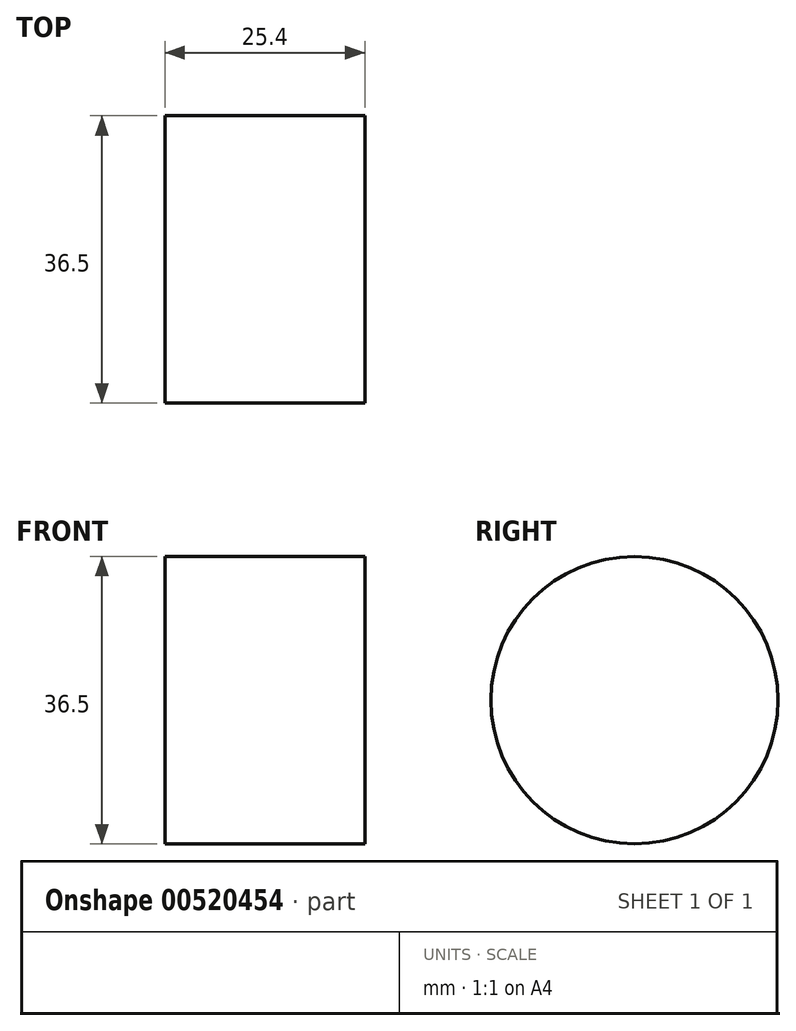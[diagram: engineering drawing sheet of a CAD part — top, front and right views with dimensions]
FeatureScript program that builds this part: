
annotation { "Feature Type Name" : "Feature", "Feature Type Description" : "" }
export const myFeature = defineFeature(function(context is Context, id is Id, definition is map)
    precondition{}
    {
        {
            var Q0;
            Q0=qCreatedBy(makeId("Right.planeOp"),FACE);
            var sketch = newSketch(context, id + "F0", { "sketchPlane" : qUnion([Q0])});
            skCircle(sketch, "E0", {"center": v(0, 0) * mm, "radius": 18.25 * mm});
            skSolve(sketch);
        }
        {
            var Q0;
            Q0 = qSketchRegion(id + "F0", true);
            extrude(context, id + "F1", {"entities" : qUnion([Q0]), "endBound" : BoundingType.SYMMETRIC, "depth" : 25.4 * mm, "offsetDistance" : 25.4 * mm});
        }
    });
